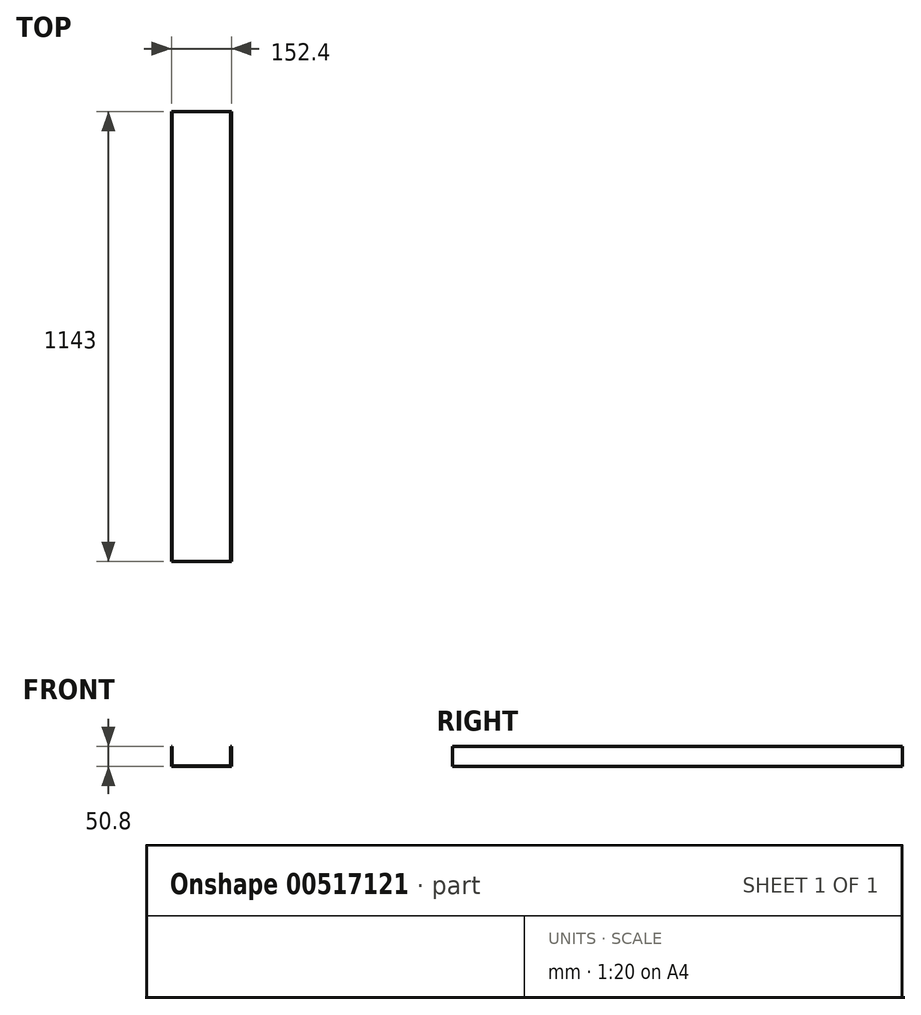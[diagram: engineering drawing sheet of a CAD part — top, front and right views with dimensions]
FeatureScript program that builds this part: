
annotation { "Feature Type Name" : "Feature", "Feature Type Description" : "" }
export const myFeature = defineFeature(function(context is Context, id is Id, definition is map)
    precondition{}
    {
        {
            var Q0;
            Q0=qCreatedBy(makeId("Front.planeOp"),FACE);
            var sketch = newSketch(context, id + "F0", { "sketchPlane" : qUnion([Q0])});
            skLineSegment(sketch, "E0", {"start": v(-43.97, 70) * mm, "end": v(-43.97, 20.8) * mm});
            skLineSegment(sketch, "E1", {"start": v(-43.97, 20.8) * mm, "end": v(105.25, 20.8) * mm});
            skLineSegment(sketch, "E2", {"start": v(105.25, 20.8) * mm, "end": v(105.25, 70) * mm});
            skLineSegment(sketch, "E3.0", {"start": v(106.84, 19.2) * mm, "end": v(106.84, 127.16) * mm});
            skLineSegment(sketch, "E3.1", {"start": v(-45.56, 19.2) * mm, "end": v(106.84, 19.2) * mm});
            skLineSegment(sketch, "E3.2", {"start": v(-45.56, 127.16) * mm, "end": v(-45.56, 19.2) * mm});
            skLineSegment(sketch, "E4", {"start": v(105.25, 70) * mm, "end": v(106.84, 70) * mm});
            skLineSegment(sketch, "E5", {"start": v(-43.97, 70) * mm, "end": v(-45.56, 70) * mm});
            skSolve(sketch);
        }
        {
            var Q0;
            Q0=makeQuery(id+"F0.imprint","IMPRINT",FACE,{"disambiguationData":[TD([[makeQuery(id+"F0.imprint","IMPRINT",EDGE,{"derivedFrom":sQuery(id+"F0.wireOp",EDGE,"E0")}),-1.0]])]});
            extrude(context, id + "F1", {"entities" : qUnion([Q0]), "depth" : 1143 * mm, "offsetDistance" : 25.4 * mm});
        }
    });
